# Revit family: 798500001_Válvula Duplex
name_source: partatom
category: Plumbing Fixtures
units: mm (PartAtom-declared; Revit-internal decimal feet)

## family parameters
Always vertical = Yes
Cut with Voids When Loaded = No
Host = Wall
OmniClass Number = 23.45.55.11
OmniClass Title = Sanitary Components
Part Type = Normal
Room Calculation Point = No
Round Connector Dimension = Use Diameter
Shared = No

## types (1)
- Type 1
    Alto = 223 mm
    Ancho = 220 mm  [stored 0.721785 ft]
    Creado por = IDD
    Dimensiones generales producto (H * W * D) = 220 x 220 x 102 mms.
· (H*L*W): 8,7 x 8,7 x 4 pulgs.
    Fabricante = Corona
    Fecha de creación = 30/07/2020
    Garantía = 1 año
    Material = Corona_Acero
    Peso Bruto aprox = 3,1 kgs. - 6,8 lbs
    Peso Neto aprox = 2,7 kgs. - 5,9 lbs
    Presion maxima = 35 - 80 PSI
    Profundidad = 102 mm  [stored 0.334646 ft]
    Temperatura de uso = 5º C a 75º C (41º F y 167º F)
    URL = https://corona.co

note: [stored X ft] marks values corroborated as IEEE doubles in the binary element streams (Revit-internal decimal feet)

## geometry (parser evidence)
native form markers: Sweep x4
no freeform markers — native parametric forms only
